annotation { "Feature Type Name" : "Feature", "Feature Type Description" : "" }
export const myFeature = defineFeature(function(context is Context, id is Id, definition is map)
    precondition{}
    {
        {
            var Q0;
            Q0=qCreatedBy(makeId("Top.planeOp"),FACE);
            var sketch = newSketch(context, id + "F0", { "sketchPlane" : qUnion([Q0])});
            skText(sketch, "E0", { "text": "OpenSans Bold", "fontName": "OpenSans-Bold.ttf"});
            skText(sketch, "E1", { "text": "Arimo Bold\n", "fontName": "Arimo-Bold.ttf"});
            skText(sketch, "E2", { "text": "DroidSansMono", "fontName": "DroidSansMono.ttf"});
            skText(sketch, "E3", { "text": "NotoSans Bold", "fontName": "NotoSansCJKsc-Bold.otf"});
            skText(sketch, "E4", { "text": "NotoSerif Bold", "fontName": "NotoSerif-Bold.ttf"});
            skText(sketch, "E5", { "text": "Tinos Bold", "fontName": "Tinos-Bold.ttf"});
            skText(sketch, "E6", { "text": "RobotoSlab Bold", "fontName": "RobotoSlab-Bold.ttf"});
            skText(sketch, "E7", { "text": "AllertaStencil", "fontName": "AllertaStencil-Regular.ttf"});
            const initialGuessF0  = {"E0": [-0.2071, -0.3232, 1, 0, 0.04032], "E1": [-0.14902, -0.10362, 1, 0, 0.04032], "E2": [-0.21683, -0.1601, 1, 0, 0.04032], "E3": [-0.20118, -0.21414, 1, 0, 0.04032], "E4": [-0.20686, -0.26696, 1, 0, 0.04032], "E5": [-0.12962, -0.44684, 1, 0, 0.04032], "E6": [-0.21651, -0.38603, 1, 0, 0.04032], "E7": [-0.19326, -0.04885, 1, 0, 0.04032]};
            skSetInitialGuess(sketch, initialGuessF0);
            skSolve(sketch);
        }
        {
            var Q0;
            Q0=qCreatedBy(makeId("Top.planeOp"),FACE);
            var sketch = newSketch(context, id + "F1", { "sketchPlane" : qUnion([Q0])});
            skLineSegment(sketch, "E8.rect.bottom", {"start": v(263.37, 15.02) * mm, "end": v(-263.37, 15.02) * mm});
            skLineSegment(sketch, "E8.rect.top", {"start": v(263.37, -472.6) * mm, "end": v(-263.37, -472.6) * mm});
            skLineSegment(sketch, "E8.rect.left", {"start": v(263.37, 15.02) * mm, "end": v(263.37, -472.6) * mm});
            skLineSegment(sketch, "E8.rect.right", {"start": v(-263.37, 15.02) * mm, "end": v(-263.37, -472.6) * mm});
            skPoint(sketch, "E8.rect.middle", {"position": v(0, -228.8) * mm});
            skSolve(sketch);
        }
        {
            var Q0;
            Q0=makeQuery(id+"F1.imprint","IMPRINT",FACE,{"disambiguationData":[TD([[makeQuery(id+"F1.imprint","IMPRINT",EDGE,{"derivedFrom":sQuery(id+"F1.wireOp",EDGE,"E8.rect.bottom")}),1.0]])]});
            extrude(context, id + "F2", {"entities" : qUnion([Q0]), "depth" : 1 * mm});
        }
        {
            var Q0;
            Q0 = qSketchRegion(id + "F0", true);
            extrude(context, id + "F3", {"entities" : qUnion([Q0]), "operationType" : NewBodyOperationType.ADD, "depth" : 4 * mm});
        }
    });